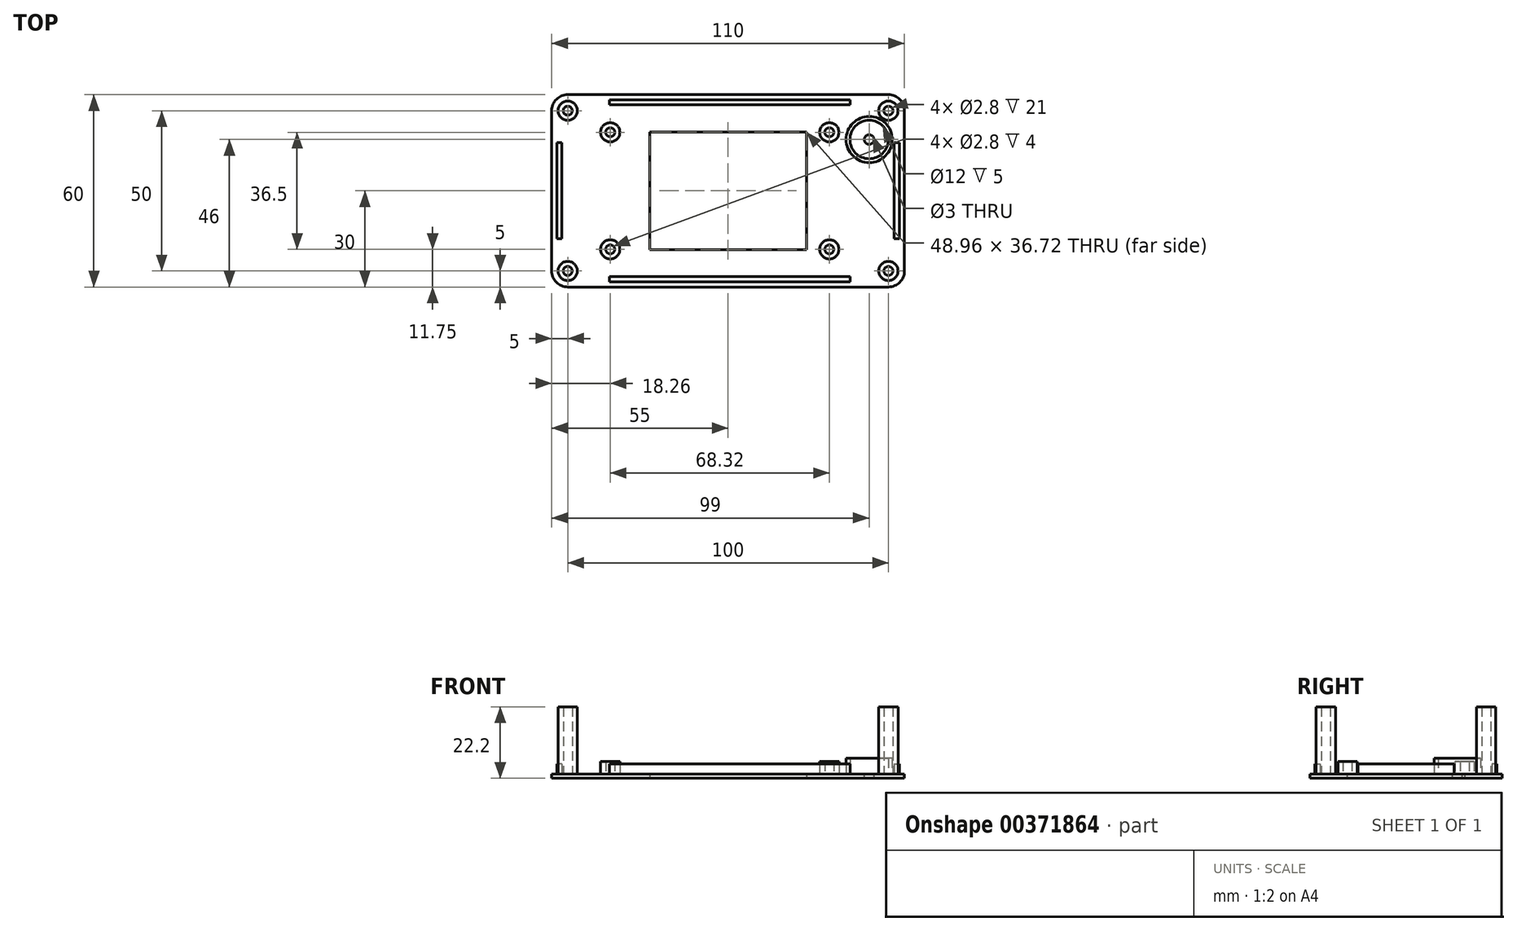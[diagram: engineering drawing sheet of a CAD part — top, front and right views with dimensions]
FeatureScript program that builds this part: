
annotation { "Feature Type Name" : "Feature", "Feature Type Description" : "" }
export const myFeature = defineFeature(function(context is Context, id is Id, definition is map)
    precondition{}
    {
        {
            var Q0;
            Q0=qCreatedBy(makeId("Top.planeOp"),FACE);
            var sketch = newSketch(context, id + "F0", { "sketchPlane" : qUnion([Q0])});
            skLineSegment(sketch, "E0.bottom", {"start": v(37.2, -21.36) * mm, "end": v(-37.2, -21.36) * mm, "construction": true});
            skLineSegment(sketch, "E0.top", {"start": v(37.2, 21.36) * mm, "end": v(-37.2, 21.36) * mm, "construction": true});
            skLineSegment(sketch, "E0.left", {"start": v(37.2, -21.36) * mm, "end": v(37.2, 21.36) * mm, "construction": true});
            skLineSegment(sketch, "E0.right", {"start": v(-37.2, -21.36) * mm, "end": v(-37.2, 21.36) * mm, "construction": true});
            skPoint(sketch, "E0.middle", {"position": v(0, 0) * mm});
            skCircle(sketch, "E1", {"center": v(-34.16, 18.25) * mm, "radius": 1.6 * mm, "construction": true});
            skCircle(sketch, "E2.MirrorC", {"center": v(34.16, 18.25) * mm, "radius": 1.6 * mm, "construction": true});
            skCircle(sketch, "E3.MirrorC", {"center": v(34.16, -18.25) * mm, "radius": 1.6 * mm, "construction": true});
            skCircle(sketch, "E4.MirrorC", {"center": v(-34.16, -18.25) * mm, "radius": 1.6 * mm, "construction": true});
            skLineSegment(sketch, "E5.bottom", {"start": v(-30.2, 21.36) * mm, "end": v(30.06, 21.36) * mm, "construction": true});
            skLineSegment(sketch, "E5.top", {"start": v(-30.2, -21.36) * mm, "end": v(30.06, -21.36) * mm, "construction": true});
            skLineSegment(sketch, "E5.left", {"start": v(-30.2, 21.36) * mm, "end": v(-30.2, -21.36) * mm, "construction": true});
            skLineSegment(sketch, "E5.right", {"start": v(30.06, 21.36) * mm, "end": v(30.06, -21.36) * mm, "construction": true});
            skLineSegment(sketch, "E6.bottom", {"start": v(-21.9, 18.36) * mm, "end": v(27.06, 18.36) * mm, "construction": true});
            skLineSegment(sketch, "E6.top", {"start": v(-21.9, -18.36) * mm, "end": v(27.06, -18.36) * mm, "construction": true});
            skLineSegment(sketch, "E6.left", {"start": v(-21.9, 18.36) * mm, "end": v(-21.9, -18.36) * mm, "construction": true});
            skLineSegment(sketch, "E6.right", {"start": v(27.06, 18.36) * mm, "end": v(27.06, -18.36) * mm, "construction": true});
            skLineSegment(sketch, "E7", {"start": v(-69.3, 0) * mm, "end": v(67.55, 0) * mm, "construction": true});
            skLineSegment(sketch, "E8", {"start": v(2.58, -33.09) * mm, "end": v(2.58, 37.46) * mm, "construction": true});
            skLineSegment(sketch, "E9.bottom", {"start": v(-21.9, 18.36) * mm, "end": v(27.06, 18.36) * mm});
            skLineSegment(sketch, "E9.top", {"start": v(-21.9, -18.36) * mm, "end": v(27.06, -18.36) * mm});
            skLineSegment(sketch, "E9.left", {"start": v(-21.9, 18.36) * mm, "end": v(-21.9, -18.36) * mm});
            skLineSegment(sketch, "E9.right", {"start": v(27.06, 18.36) * mm, "end": v(27.06, -18.36) * mm});
            skLineSegment(sketch, "E10.bottom", {"start": v(57.58, -30) * mm, "end": v(-52.42, -30) * mm});
            skLineSegment(sketch, "E10.top", {"start": v(57.58, 30) * mm, "end": v(-52.42, 30) * mm});
            skLineSegment(sketch, "E10.left", {"start": v(57.58, -30) * mm, "end": v(57.58, 30) * mm});
            skLineSegment(sketch, "E10.right", {"start": v(-52.42, -30) * mm, "end": v(-52.42, 30) * mm});
            skPoint(sketch, "E10.middle", {"position": v(2.58, 0) * mm});
            skSolve(sketch);
        }
        {
            var Q0;
            Q0=makeQuery(id+"F0.imprint","IMPRINT",FACE,{"disambiguationData":[TD([[makeQuery(id+"F0.imprint","IMPRINT",EDGE,{"derivedFrom":sQuery(id+"F0.wireOp",EDGE,"E9.bottom")}),1.0]])]});
            extrude(context, id + "F1", {"entities" : qUnion([Q0]), "depth" : 1.2 * mm});
        }
        {
            var Q0;
            Q0=makeQuery(id+"F1.opExtrude","CAP_FACE",FACE,{"disambiguationData":[OSD([sQuery(id+"F0.wireOp",EDGE,"E9.bottom"),sQuery(id+"F0.wireOp",EDGE,"E9.top"),sQuery(id+"F0.wireOp",EDGE,"E9.left"),sQuery(id+"F0.wireOp",EDGE,"E9.right"),sQuery(id+"F0.wireOp",EDGE,"E10.bottom"),sQuery(id+"F0.wireOp",EDGE,"E10.top"),sQuery(id+"F0.wireOp",EDGE,"E10.left"),sQuery(id+"F0.wireOp",EDGE,"E10.right"),sQuery(id+"F0.wireOp",EDGE,"zpZsg9xE-iQUr-hMDx-4yTp-kwfv9a1k3Hto"),sQuery(id+"F0.wireOp",EDGE,"v62mlMx0-zebu-okq2-FoMi-auxJvthpUieG"),sQuery(id+"F0.wireOp",EDGE,"qMjBRCcc-lWBf-kRpo-uLkv-zHoKJKTILuRE"),sQuery(id+"F0.wireOp",EDGE,"fnRMTj3t-sgWX-KTiA-dPVG-LLRJFn4VET2m")])],"isStart":false});
            var sketch = newSketch(context, id + "F2", { "sketchPlane" : qUnion([Q0])});
            skCircle(sketch, "E11", {"center": v(46.58, 16) * mm, "radius": 7.2 * mm});
            skCircle(sketch, "E12", {"center": v(46.58, 16) * mm, "radius": 6 * mm});
            skSolve(sketch);
        }
        {
            var Q0;
            Q0 = qSketchRegion(id + "F2", true);
            extrude(context, id + "F3", {"entities" : qUnion([Q0]), "operationType" : NewBodyOperationType.ADD, "depth" : 5 * mm});
        }
        {
            var Q0;
            Q0 = qSketchRegion(id + "F2", true);
            extrude(context, id + "F4", {"entities" : qUnion([Q0]), "operationType" : NewBodyOperationType.ADD, "depth" : 5 * mm});
        }
        {
            var Q0;
            Q0=makeQuery(id+"F3.boolean.opBoolean","SPLIT",FACE,{"disambiguationData":[TD([makeQuery(id+"F3.opExtrude","SWEPT_FACE",FACE,{"disambiguationData":[OSD([sQuery(id+"F2.wireOp",EDGE,"E12")])]})])],"derivedFrom":makeQuery(id+"F1.opExtrude","CAP_FACE",FACE,{"disambiguationData":[OSD([sQuery(id+"F0.wireOp",EDGE,"E9.bottom"),sQuery(id+"F0.wireOp",EDGE,"E9.top"),sQuery(id+"F0.wireOp",EDGE,"E9.left"),sQuery(id+"F0.wireOp",EDGE,"E9.right"),sQuery(id+"F0.wireOp",EDGE,"E10.bottom"),sQuery(id+"F0.wireOp",EDGE,"E10.top"),sQuery(id+"F0.wireOp",EDGE,"E10.left"),sQuery(id+"F0.wireOp",EDGE,"E10.right"),sQuery(id+"F0.wireOp",EDGE,"zpZsg9xE-iQUr-hMDx-4yTp-kwfv9a1k3Hto"),sQuery(id+"F0.wireOp",EDGE,"v62mlMx0-zebu-okq2-FoMi-auxJvthpUieG"),sQuery(id+"F0.wireOp",EDGE,"qMjBRCcc-lWBf-kRpo-uLkv-zHoKJKTILuRE"),sQuery(id+"F0.wireOp",EDGE,"fnRMTj3t-sgWX-KTiA-dPVG-LLRJFn4VET2m")])],"isStart":false})});
            var sketch = newSketch(context, id + "F5", { "sketchPlane" : qUnion([Q0])});
            skCircle(sketch, "E13", {"center": v(46.58, 16) * mm, "radius": 1.5 * mm});
            skSolve(sketch);
        }
        {
            var Q0;
            Q0 = qSketchRegion(id + "F5", true);
            extrude(context, id + "F6", {"entities" : qUnion([Q0]), "operationType" : NewBodyOperationType.REMOVE, "oppositeDirection" : true, "depth" : 25 * mm});
        }
        {
            var Q0;
            Q0=makeQuery(id+"F1.opExtrude","SWEPT_EDGE",EDGE,{"disambiguationData":[OSD([sQuery(id+"F0.wireOp",EDGE,"E10.top"),sQuery(id+"F0.wireOp",EDGE,"E10.left")])]});
            var Q1;
            Q1=makeQuery(id+"F1.opExtrude","SWEPT_EDGE",EDGE,{"disambiguationData":[OSD([sQuery(id+"F0.wireOp",EDGE,"E10.top"),sQuery(id+"F0.wireOp",EDGE,"E10.right")])]});
            var Q2;
            Q2=makeQuery(id+"F1.opExtrude","SWEPT_EDGE",EDGE,{"disambiguationData":[OSD([sQuery(id+"F0.wireOp",EDGE,"E10.bottom"),sQuery(id+"F0.wireOp",EDGE,"E10.right")])]});
            var Q3;
            Q3=makeQuery(id+"F1.opExtrude","SWEPT_EDGE",EDGE,{"disambiguationData":[OSD([sQuery(id+"F0.wireOp",EDGE,"E10.bottom"),sQuery(id+"F0.wireOp",EDGE,"E10.left")])]});
            fillet(context, id + "F7", {"entities" : qUnion([Q0, Q1, Q2, Q3]), "radius" : 5 * mm, "tangentPropagation" : true, "allowEdgeOverflow" : false});
        }
        {
            var Q0;
            {var subQ0=sQuery(id+"F0.wireOp",EDGE,"zpZsg9xE-iQUr-hMDx-4yTp-kwfv9a1k3Hto");var subQ1=sQuery(id+"F0.wireOp",EDGE,"E10.right");var subQ2=sQuery(id+"F0.wireOp",EDGE,"E10.left");var subQ3=sQuery(id+"F0.wireOp",EDGE,"E10.top");var subQ4=sQuery(id+"F0.wireOp",EDGE,"E10.bottom");var subQ5=sQuery(id+"F0.wireOp",EDGE,"v62mlMx0-zebu-okq2-FoMi-auxJvthpUieG");var subQ6=sQuery(id+"F0.wireOp",EDGE,"E9.bottom");var subQ7=sQuery(id+"F0.wireOp",EDGE,"E9.right");var subQ8=sQuery(id+"F0.wireOp",EDGE,"E9.top");var subQ9=sQuery(id+"F0.wireOp",EDGE,"E9.left");var subQ10=sQuery(id+"F0.wireOp",EDGE,"qMjBRCcc-lWBf-kRpo-uLkv-zHoKJKTILuRE");var subQ11=sQuery(id+"F0.wireOp",EDGE,"fnRMTj3t-sgWX-KTiA-dPVG-LLRJFn4VET2m");Q0=makeQuery(id+"F3.boolean.opBoolean","SPLIT",FACE,{"disambiguationData":[TD([makeQuery(id+"F1.opExtrude","SWEPT_FACE",FACE,{"disambiguationData":[OSD([subQ6])]})])],"derivedFrom":makeQuery(id+"F1.opExtrude","CAP_FACE",FACE,{"disambiguationData":[OSD([subQ6,subQ8,subQ9,subQ7,subQ4,subQ3,subQ2,subQ1,subQ0,subQ5,subQ10,subQ11])],"isStart":false})});}
            var sketch = newSketch(context, id + "F8", { "sketchPlane" : qUnion([Q0])});
            skLineSegment(sketch, "E14.bottom", {"start": v(52.58, -25) * mm, "end": v(-47.42, -25) * mm, "construction": true});
            skLineSegment(sketch, "E14.top", {"start": v(52.58, 25) * mm, "end": v(-47.42, 25) * mm, "construction": true});
            skLineSegment(sketch, "E14.left", {"start": v(52.58, -25) * mm, "end": v(52.58, 25) * mm, "construction": true});
            skLineSegment(sketch, "E14.right", {"start": v(-47.42, -25) * mm, "end": v(-47.42, 25) * mm, "construction": true});
            skCircle(sketch, "E15", {"center": v(52.58, 25) * mm, "radius": 3 * mm});
            skCircle(sketch, "E16", {"center": v(52.58, -25) * mm, "radius": 3 * mm});
            skCircle(sketch, "E17", {"center": v(-47.42, -25) * mm, "radius": 3 * mm});
            skCircle(sketch, "E18", {"center": v(-47.42, 25) * mm, "radius": 3 * mm});
            skCircle(sketch, "E19", {"center": v(52.58, -25) * mm, "radius": 1.4 * mm});
            skCircle(sketch, "E20", {"center": v(-47.42, -25) * mm, "radius": 1.4 * mm});
            skCircle(sketch, "E21", {"center": v(52.58, 25) * mm, "radius": 1.4 * mm});
            skCircle(sketch, "E22", {"center": v(-47.42, 25) * mm, "radius": 1.4 * mm});
            skSolve(sketch);
        }
        {
            var Q0;
            Q0 = qSketchRegion(id + "F8", true);
            extrude(context, id + "F9", {"entities" : qUnion([Q0]), "operationType" : NewBodyOperationType.ADD, "depth" : 21 * mm});
        }
        {
            var Q0;
            {var subQ1=sQuery(id+"F0.wireOp",EDGE,"E9.left");var subQ3=sQuery(id+"F0.wireOp",EDGE,"E10.left");var subQ4=sQuery(id+"F0.wireOp",EDGE,"E10.top");var subQ5=sQuery(id+"F0.wireOp",EDGE,"E10.right");var subQ7=sQuery(id+"F0.wireOp",EDGE,"E10.bottom");var subQ11=sQuery(id+"F0.wireOp",EDGE,"E9.bottom");var subQ12=makeQuery(id+"F1.opExtrude","SWEPT_FACE",FACE,{"disambiguationData":[OSD([subQ11])]});var subQ13=sQuery(id+"F0.wireOp",EDGE,"E9.right");var subQ15=sQuery(id+"F0.wireOp",EDGE,"E9.top");Q0=makeQuery(id+"F9.boolean.opBoolean","SPLIT",FACE,{"disambiguationData":[TD([subQ12])],"derivedFrom":makeQuery(id+"F3.boolean.opBoolean","SPLIT",FACE,{"disambiguationData":[TD([subQ12])],"derivedFrom":makeQuery(id+"F1.opExtrude","CAP_FACE",FACE,{"disambiguationData":[OSD([subQ11,subQ15,subQ1,subQ13,subQ7,subQ4,subQ3,subQ5])],"isStart":false})})});}
            var sketch = newSketch(context, id + "F10", { "sketchPlane" : qUnion([Q0])});
            skCircle(sketch, "E23", {"center": v(34.16, -18.25) * mm, "radius": 3 * mm});
            skCircle(sketch, "E24", {"center": v(-34.16, -18.25) * mm, "radius": 3 * mm});
            skCircle(sketch, "E25", {"center": v(34.16, 18.25) * mm, "radius": 3 * mm});
            skCircle(sketch, "E26", {"center": v(-34.16, 18.25) * mm, "radius": 3 * mm});
            skCircle(sketch, "E27", {"center": v(-34.16, -18.25) * mm, "radius": 1.4 * mm});
            skCircle(sketch, "E28", {"center": v(-34.16, 18.25) * mm, "radius": 1.4 * mm});
            skCircle(sketch, "E29", {"center": v(34.16, -18.25) * mm, "radius": 1.4 * mm});
            skCircle(sketch, "E30", {"center": v(34.16, 18.25) * mm, "radius": 1.4 * mm});
            skSolve(sketch);
        }
        {
            var Q0;
            Q0 = qSketchRegion(id + "F10", true);
            extrude(context, id + "F11", {"entities" : qUnion([Q0]), "operationType" : NewBodyOperationType.ADD, "depth" : 4 * mm});
        }
        {
            var Q0;
            {var subQ1=sQuery(id+"F0.wireOp",EDGE,"E9.left");var subQ3=sQuery(id+"F0.wireOp",EDGE,"E10.left");var subQ4=sQuery(id+"F0.wireOp",EDGE,"E10.top");var subQ6=sQuery(id+"F0.wireOp",EDGE,"E10.right");var subQ9=sQuery(id+"F0.wireOp",EDGE,"E10.bottom");var subQ15=sQuery(id+"F0.wireOp",EDGE,"E9.bottom");var subQ16=makeQuery(id+"F1.opExtrude","SWEPT_FACE",FACE,{"disambiguationData":[OSD([subQ15])]});var subQ17=sQuery(id+"F0.wireOp",EDGE,"E9.right");var subQ20=sQuery(id+"F0.wireOp",EDGE,"E9.top");Q0=makeQuery(id+"F11.boolean.opBoolean","SPLIT",FACE,{"disambiguationData":[TD([subQ16])],"derivedFrom":makeQuery(id+"F9.boolean.opBoolean","SPLIT",FACE,{"disambiguationData":[TD([subQ16])],"derivedFrom":makeQuery(id+"F3.boolean.opBoolean","SPLIT",FACE,{"disambiguationData":[TD([subQ16])],"derivedFrom":makeQuery(id+"F1.opExtrude","CAP_FACE",FACE,{"disambiguationData":[OSD([subQ15,subQ20,subQ1,subQ17,subQ9,subQ4,subQ3,subQ6])],"isStart":false})})})});}
            var sketch = newSketch(context, id + "F12", { "sketchPlane" : qUnion([Q0])});
            skLineSegment(sketch, "E31.bottom", {"start": v(40.62, -28.4) * mm, "end": v(-34.38, -28.4) * mm});
            skLineSegment(sketch, "E31.top", {"start": v(40.62, -26.8) * mm, "end": v(-34.38, -26.8) * mm});
            skLineSegment(sketch, "E31.left", {"start": v(40.62, -28.4) * mm, "end": v(40.62, -26.8) * mm});
            skLineSegment(sketch, "E31.right", {"start": v(-34.38, -28.4) * mm, "end": v(-34.38, -26.8) * mm});
            skPoint(sketch, "E31.middle", {"position": v(3.12, -27.6) * mm});
            skLineSegment(sketch, "E32.MirrorCS", {"start": v(40.62, 26.8) * mm, "end": v(-34.38, 26.8) * mm});
            skLineSegment(sketch, "E33.MirrorCS", {"start": v(40.62, 28.4) * mm, "end": v(-34.38, 28.4) * mm});
            skLineSegment(sketch, "E34.MirrorCS", {"start": v(-34.38, 28.4) * mm, "end": v(-34.38, 26.8) * mm});
            skLineSegment(sketch, "E35.MirrorCS", {"start": v(40.62, 28.4) * mm, "end": v(40.62, 26.8) * mm});
            skLineSegment(sketch, "E36.bottom", {"start": v(-49.22, -15) * mm, "end": v(-50.82, -15) * mm});
            skLineSegment(sketch, "E36.top", {"start": v(-49.22, 15) * mm, "end": v(-50.82, 15) * mm});
            skLineSegment(sketch, "E36.left", {"start": v(-49.22, -15) * mm, "end": v(-49.22, 15) * mm});
            skLineSegment(sketch, "E36.right", {"start": v(-50.82, -15) * mm, "end": v(-50.82, 15) * mm});
            skPoint(sketch, "E36.middle", {"position": v(-50.02, 0) * mm});
            skLineSegment(sketch, "E37.MirrorCS", {"start": v(54.38, -15) * mm, "end": v(54.38, 15) * mm});
            skLineSegment(sketch, "E38.MirrorCS", {"start": v(55.98, -15) * mm, "end": v(55.98, 15) * mm});
            skLineSegment(sketch, "E39.MirrorCS", {"start": v(54.38, 15) * mm, "end": v(55.98, 15) * mm});
            skLineSegment(sketch, "E40.MirrorCS", {"start": v(54.38, -15) * mm, "end": v(55.98, -15) * mm});
            skSolve(sketch);
        }
        {
            var Q0;
            Q0 = qSketchRegion(id + "F12", true);
            extrude(context, id + "F13", {"entities" : qUnion([Q0]), "operationType" : NewBodyOperationType.ADD, "depth" : 3.2 * mm});
        }
    });
